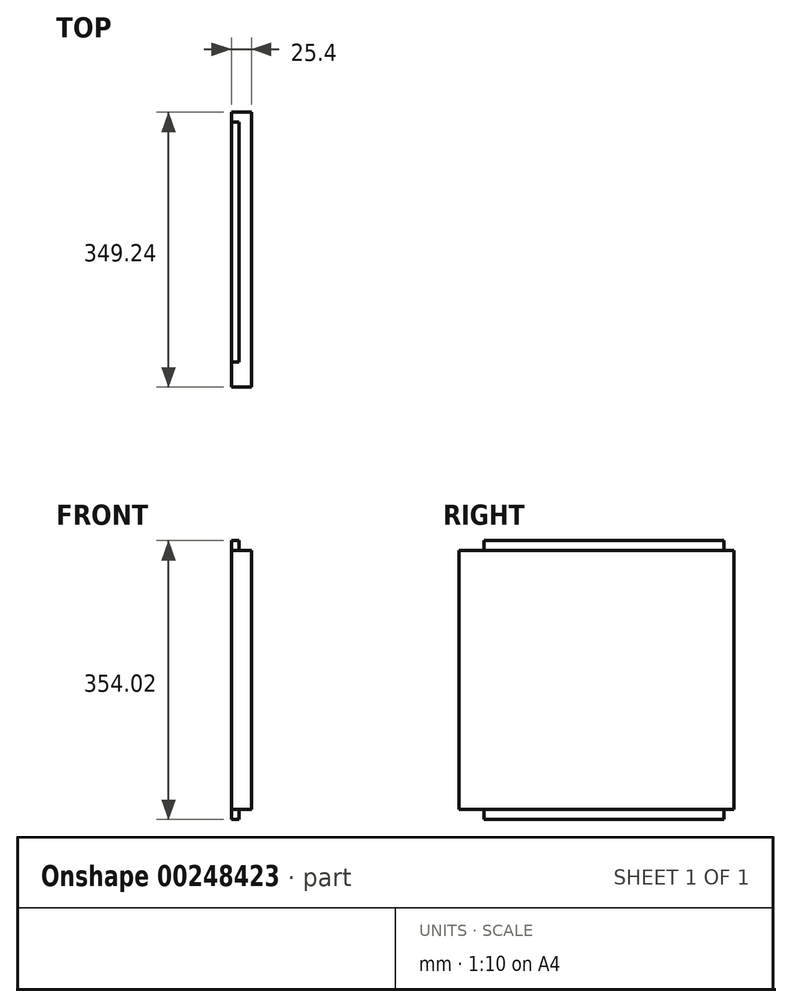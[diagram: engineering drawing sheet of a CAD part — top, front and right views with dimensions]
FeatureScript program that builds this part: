
annotation { "Feature Type Name" : "Feature", "Feature Type Description" : "" }
export const myFeature = defineFeature(function(context is Context, id is Id, definition is map)
    precondition{}
    {
        {
            var Q0;
            Q0=qCreatedBy(makeId("Right.planeOp"),FACE);
            var sketch = newSketch(context, id + "F0", { "sketchPlane" : qUnion([Q0])});
            skLineSegment(sketch, "E0.bottom", {"start": v(-174.62, 164.3) * mm, "end": v(174.63, 164.3) * mm});
            skLineSegment(sketch, "E0.top", {"start": v(-174.63, -164.3) * mm, "end": v(174.62, -164.3) * mm});
            skLineSegment(sketch, "E0.left", {"start": v(-174.62, 164.3) * mm, "end": v(-174.63, -164.3) * mm});
            skLineSegment(sketch, "E0.right", {"start": v(174.63, 164.3) * mm, "end": v(174.62, -164.3) * mm});
            skPoint(sketch, "E0.middle", {"position": v(0, 0) * mm});
            skSolve(sketch);
        }
        {
            var Q0;
            Q0=qSketchRegion(id+"F0",true);
            extrude(context, id + "F1", {"entities" : qUnion([Q0]), "endBound" : BoundingType.SYMMETRIC, "depth" : 25.4 * mm});
        }
        {
            var Q0;
            Q0=makeQuery(id+"F1.opExtrude","SWEPT_FACE",FACE,{"disambiguationData":[OSD([sQuery(id+"F0.wireOp",EDGE,"E0.bottom")])]});
            var sketch = newSketch(context, id + "F2", { "sketchPlane" : qUnion([Q0])});
            skLineSegment(sketch, "E1", {"start": v(-3.18, 161.93) * mm, "end": v(-3.17, -142.88) * mm});
            skLineSegment(sketch, "E2", {"start": v(-3.18, 161.93) * mm, "end": v(-12.7, 161.93) * mm});
            skLineSegment(sketch, "E3", {"start": v(-3.17, -142.88) * mm, "end": v(-12.7, -142.88) * mm});
            skLineSegment(sketch, "E4", {"start": v(-12.7, 161.93) * mm, "end": v(-12.7, -142.88) * mm});
            skPoint(sketch, "E5.orphan", {"position": v(-3.18, 174.63) * mm});
            skSolve(sketch);
        }
        {
            var Q0;
            Q0=makeQuery(id+"F2.imprint","IMPRINT",FACE,{"disambiguationData":[TD([[makeQuery(id+"F2.imprint","IMPRINT",EDGE,{"derivedFrom":sQuery(id+"F2.wireOp",EDGE,"E1")}),-1.0]])]});
            extrude(context, id + "F3", {"entities" : qUnion([Q0]), "operationType" : NewBodyOperationType.ADD, "depth" : 12.7 * mm});
        }
        {
            var Q0;
            Q0=makeQuery(id+"F1.opExtrude","SWEPT_FACE",FACE,{"disambiguationData":[OSD([sQuery(id+"F0.wireOp",EDGE,"E0.top")])]});
            var sketch = newSketch(context, id + "F4", { "sketchPlane" : qUnion([Q0])});
            skLineSegment(sketch, "E6", {"start": v(-3.18, 142.88) * mm, "end": v(-3.18, -161.93) * mm});
            skLineSegment(sketch, "E7", {"start": v(-3.18, 142.88) * mm, "end": v(-12.7, 142.88) * mm});
            skLineSegment(sketch, "E8", {"start": v(-12.7, -161.93) * mm, "end": v(-3.17, -161.93) * mm});
            skLineSegment(sketch, "E9", {"start": v(-12.7, -161.93) * mm, "end": v(-12.7, 142.88) * mm});
            skSolve(sketch);
        }
        {
            var Q0;
            Q0=makeQuery(id+"F4.imprint","IMPRINT",FACE,{"disambiguationData":[TD([[makeQuery(id+"F4.imprint","IMPRINT",EDGE,{"derivedFrom":sQuery(id+"F4.wireOp",EDGE,"E6")}),-1.0]])]});
            extrude(context, id + "F5", {"entities" : qUnion([Q0]), "operationType" : NewBodyOperationType.ADD, "depth" : 12.7 * mm});
        }
    });
